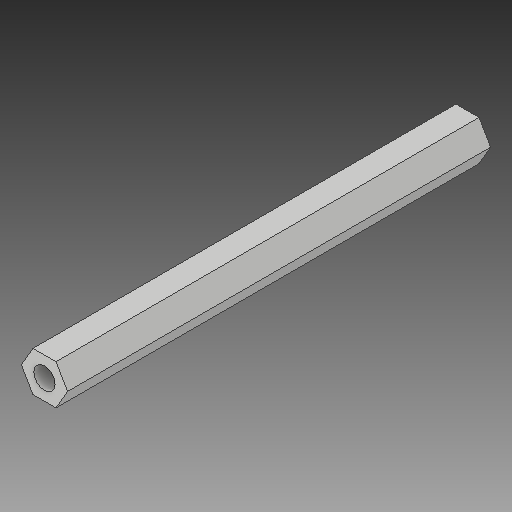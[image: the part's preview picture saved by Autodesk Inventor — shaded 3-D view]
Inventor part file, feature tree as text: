
AUTODESK INVENTOR PART (.ipt)
format: ipt  version: 2017 (Build 210142000, 142)  size: 104,960 bytes
history: native  units: in
note: dims shown in document units (in); Inventor stores cm internally (conversion verified against a paired STEP export)
features: other x3, sketch x1
ambient origin geometry x8: Origin, YZ Plane, XZ Plane, XY Plane, X Axis, Y Axis, Z Axis, Center Point
bodies: Solid1 (feature_tree)
feature tree (4):
  other  "Back_Wheel_Hex_Shaft.ipt"
  other  "Solid1::Back_Wheel_Hex_Shaft.ipt"
  other  "TaggingFeature1"
  sketch  "Sketch1"  dims[d0=0.3937in]
